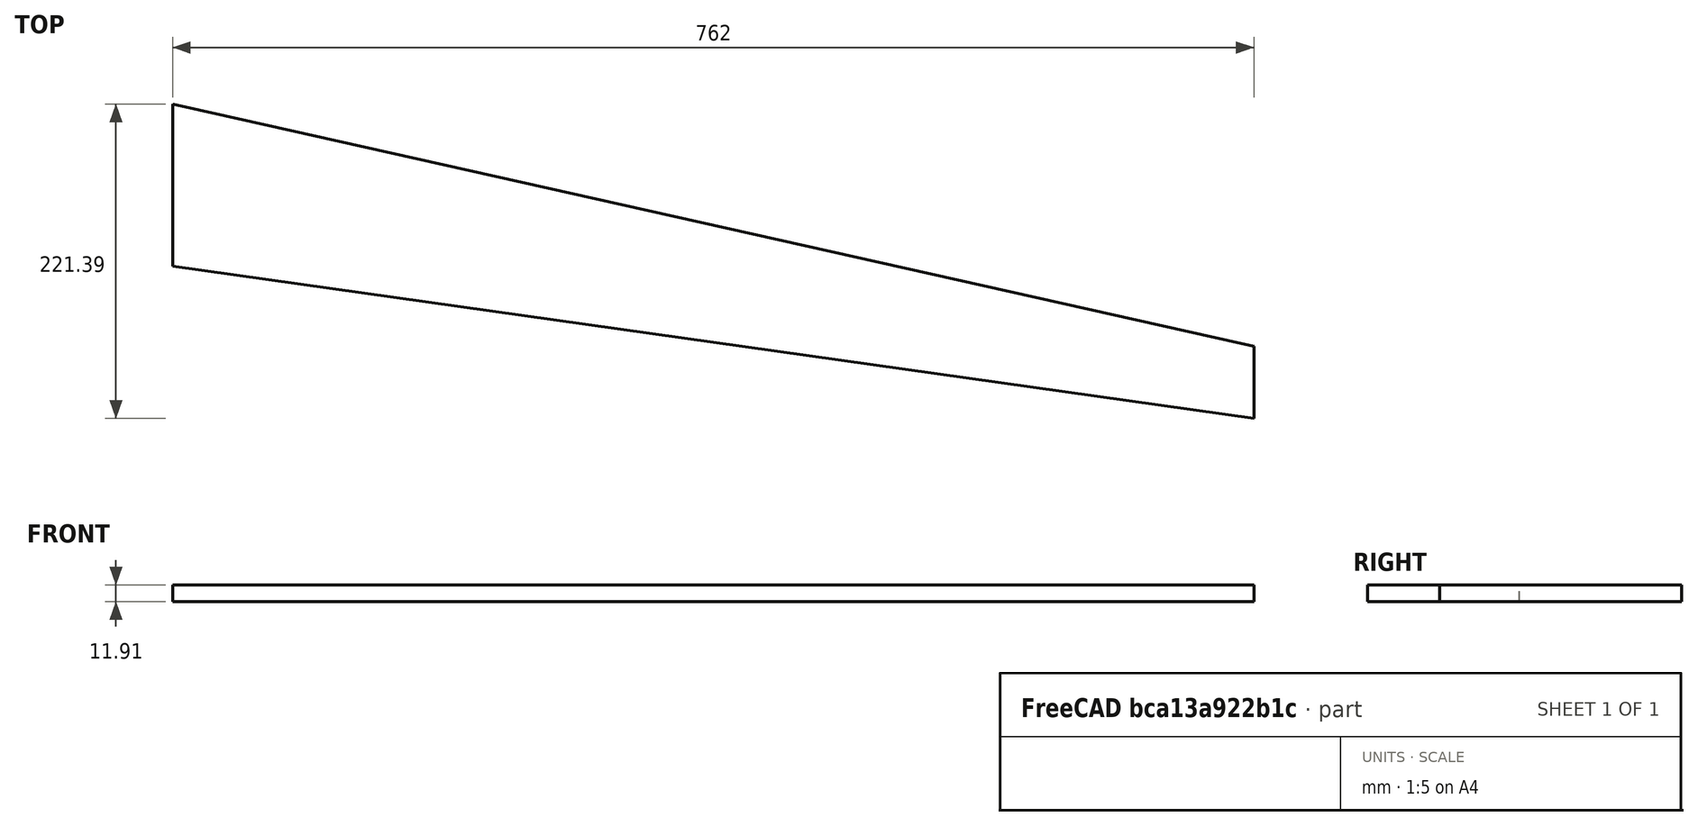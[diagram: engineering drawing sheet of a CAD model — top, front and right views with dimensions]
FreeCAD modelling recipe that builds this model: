
FCSTD DOCUMENT  (FreeCAD 0.20R29603 (Git))
Label: Leg
License: All rights reserved
LicenseURL: http://en.wikipedia.org/wiki/All_rights_reserved
objects: App::DocumentObjectGroup×3, Sketcher::SketchObject×1, PartDesign::Pad×1, PartDesign::Body×1, PartDesign::CoordinateSystem×1, App::FeaturePython×1, App::Part×1
note: 5 computed .brp shape members not serialized (recipe doc carries the construction recipe); baked Part::Feature solids carry a one-line shape summary decoded from their .brp
EXTERNAL_REF file=Parameters.FCStd obj=Spreadsheet

FEATURE [Sketcher::SketchObject] Sketch
  FullyConstrained = false
  MapMode = 5
  Support = -> [XY_Plane]
  expr: Constraints[10] = <<Parameters>>#<<DeskDimensions>>.Leg_Top
  expr: Constraints[16] = <<Parameters>>#<<DeskDimensions>>.Leg_Bottom
  expr: Constraints[5] = <<Parameters>>#<<DeskDimensions>>.Leg_Length
  sketch-geometry (8):
    g0: LineSegment StartX=0 StartY=114.3 StartZ=0 EndX=0 EndY=0 EndZ=0
    g1: LineSegment StartX=0 StartY=0 StartZ=0 EndX=762 EndY=-107.092 EndZ=0
    g2: LineSegment StartX=0 StartY=-107.092 StartZ=0 EndX=762 EndY=-107.092 EndZ=0
    g3: LineSegment StartX=762 StartY=-107.092 StartZ=0 EndX=762 EndY=534.568 EndZ=0
    g4: LineSegment StartX=762 StartY=534.568 StartZ=0 EndX=0 EndY=534.568 EndZ=0
    g5: LineSegment StartX=0 StartY=534.568 StartZ=0 EndX=0 EndY=-107.092 EndZ=0
    g6: LineSegment StartX=762 StartY=-107.092 StartZ=0 EndX=762 EndY=-56.2921 EndZ=0
    g7: LineSegment StartX=762 StartY=-56.2921 StartZ=0 EndX=0 EndY=114.3 EndZ=0
  constraints (22):
    c: Coincident(g4,g5)
    c: Coincident(g5,g2)
    c: Horizontal(g4)
    c: Vertical(g3)
    c: Vertical(g5)
    c: DistanceX(g4,g4) = 762
    c: Coincident(g1,g2)
    c: Angle(g1,g0) = 1.71042
    c: Horizontal(g2)
    c: Vertical(g0)
    c: DistanceY(g0,g0) = 114.3
    c: PointOnObject(g0,g5)
    c: Coincident(g6,g1)
    c: Vertical(g6)
    c: Coincident(g7,g6)
    c: Coincident(g7,g0)
    c: DistanceY(g6,g6) = 50.8
    c: Coincident(g3,g1)
    c: Coincident(g4,g3)
    c: Coincident(g1,g0)
    c: DistanceX(g0) = 0
    c: DistanceY(g0) = 0
FEATURE [PartDesign::Pad] Pad
  Direction = (0,0,1)
  Length = 11.9062
  Length2 = 10
  Profile = -> Sketch
  ReferenceAxis = -> Sketch [N_Axis]
  Type = 0
  expr: Length = <<Parameters>>#<<DeskDimensions>>.Stock_Thickness
FEATURE [PartDesign::Body] Body
  Group = -> [Sketch,Pad]
  Origin = -> Origin
  Tip = -> Pad
FEATURE [App::DocumentObjectGroup] Parts
FEATURE [PartDesign::CoordinateSystem] LCS_Origin
  AttacherType = Attacher::AttachEngine3D
  MapMode = 2
  Support = -> [X_Axis001]
FEATURE [App::DocumentObjectGroup] Constraints
FEATURE [App::FeaturePython] Variables  # WARN: FeaturePython — macro-defined, semantics opaque (R4)
  Type = App::PropertyContainer
FEATURE [App::DocumentObjectGroup] Configurations
FEATURE [App::Part] Model
  Group = -> [LCS_Origin,Constraints,Variables,Configurations,Body]
  Origin = -> Origin001
  Type = Assembly
